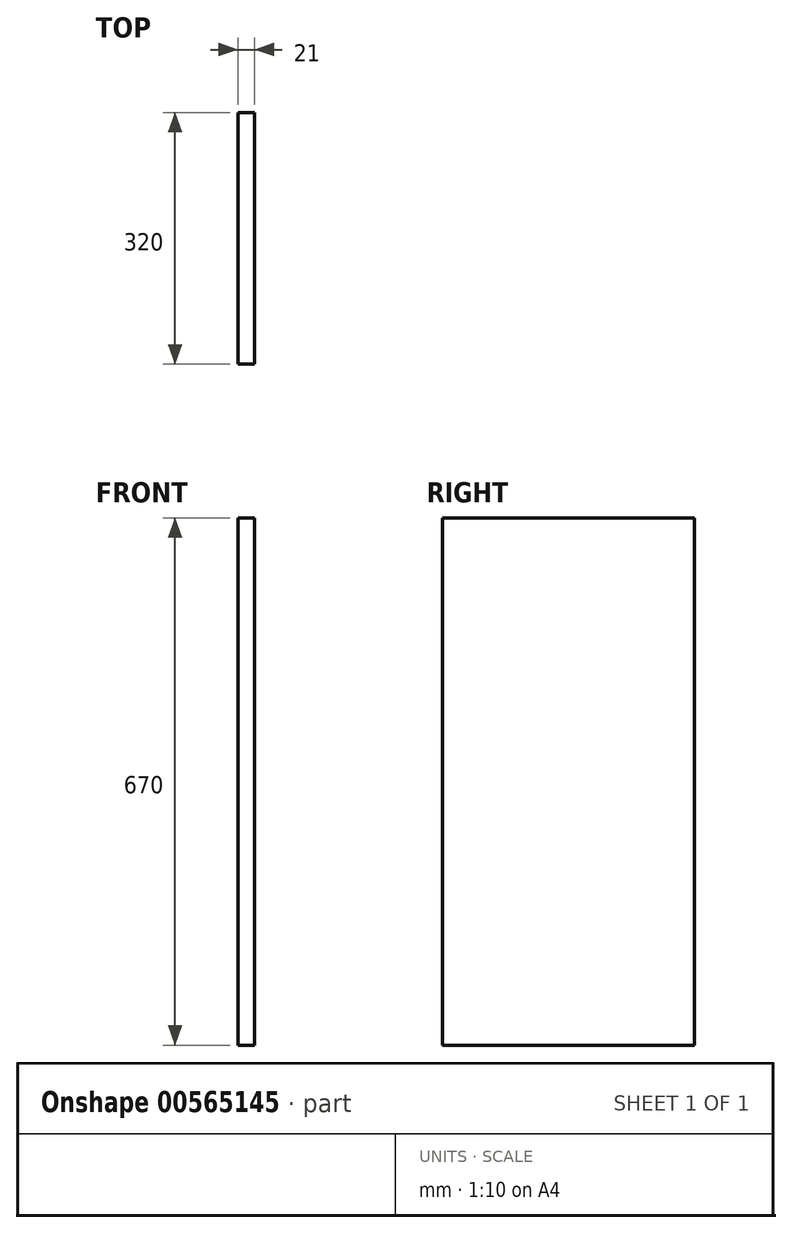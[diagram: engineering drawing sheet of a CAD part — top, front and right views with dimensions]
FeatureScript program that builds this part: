
annotation { "Feature Type Name" : "Feature", "Feature Type Description" : "" }
export const myFeature = defineFeature(function(context is Context, id is Id, definition is map)
    precondition{}
    {
        {
            var Q0;
            Q0=qCreatedBy(makeId("Right.planeOp"),FACE);
            var sketch = newSketch(context, id + "F0", { "sketchPlane" : qUnion([Q0])});
            skLineSegment(sketch, "E0.bottom", {"start": v(-160, 335) * mm, "end": v(160, 335) * mm});
            skLineSegment(sketch, "E0.top", {"start": v(-160, -335) * mm, "end": v(160, -335) * mm});
            skLineSegment(sketch, "E0.left", {"start": v(-160, 335) * mm, "end": v(-160, -335) * mm});
            skLineSegment(sketch, "E0.right", {"start": v(160, 335) * mm, "end": v(160, -335) * mm});
            skPoint(sketch, "E0.middle", {"position": v(0, 0) * mm});
            skSolve(sketch);
        }
        {
            var Q0;
            Q0 = qSketchRegion(id + "F0", true);
            var Q1;
            Q1=makeQuery(id+"F0.imprint","IMPRINT",FACE,{"disambiguationData":[TD([[makeQuery(id+"F0.imprint","IMPRINT",EDGE,{"derivedFrom":sQuery(id+"F0.wireOp",EDGE,"E0.bottom")}),-1.0]])]});
            extrude(context, id + "F1", {"entities" : qUnion([Q0, Q1]), "depth" : 21 * mm, "offsetDistance" : 25 * mm});
        }
    });
